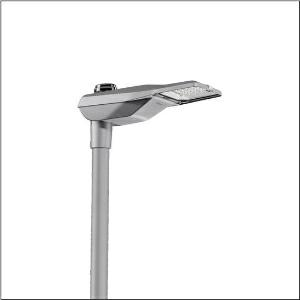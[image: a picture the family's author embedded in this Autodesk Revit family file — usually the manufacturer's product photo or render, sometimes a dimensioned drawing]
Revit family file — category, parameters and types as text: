
# Revit family: streetlight_sl_21_micro___st1_0a_5xe5d37n08db_4323
name_source: partatom
category: Lighting Fixtures
units: mm (PartAtom-declared; Revit-internal decimal feet)

## family parameters
Cut with Voids When Loaded = No
Host = Face
Light Source = No
Part Type = Normal
Room Calculation Point = No
Round Connector Dimension = Use Diameter
Shared = No

## types (1)
- --- (1 x LED, 5110 lm, 39.1 W, 3000K)
    Apparent Load = 39 VA
    CIE Flux Codes = 37 72 97 100 100
    Color Rendering = 70
    Color Temperature = 3000K
    Default Elevation = 1800 mm
    Description = Streetlight SL 21 micro, mast luminaire, primary light control with lens, of PMMA, primary optical cover: cover, of toughened safety glass, transparent, light distribution: ST1.0a, light emission: direct distribution, primary light characteristic: asymmetric, installation type: post-top, LED, 3G 1.5mm², High Power LED, rated luminous flux: 5.110lm, luminous efficacy: 131lm/W, light colour: 730, colour temperature: 3000K, control: overheat protection, presetting dimming linear, constant luminous flux control, time-dependent luminous flux control, flexible luminous flux parameterisation, mains connection: 230..240V, AC, 50/60Hz, connection cable pre-assembled, cable length: 6,5m, wiring characteristics: H07RN-F, start of lifetime: 39W, end of service life: 41W, reduction: 18W, luminaire housing, of diecast aluminium (EN AC-44300), powder-coated, Siteco® metallic grey (DB 702S), corrosivity category C5 mid according to DIN EN ISO 12944, multi-level sealing system, sealing non-destructively replaceable, inclination adjustable: 0°, 5°, 10°, 15°, length: 528mm, width: 235mm, height: 110mm, spigot size: 76/60mm (post-top), protection rating (complete): IP66, insulation class (complete): insulation class I (protective earthing), certification: CE, ENEC, ENEC+, VDE, impact resistance: IK09, permissible operating ambient temperature for outdoor applications: -40..+50°C, standard-compliant lighting for roads and squares, packaging unit: 1 piece

Light Distribution: ST1.0a
    Height = 110 mm
    Lamp = 1 x LED
    Lamp Light Flux = 5110 lm
    Lamp Power = 39.1 W
    Lamp count = 1
    Length = 528 mm
    Luminous efficacy = 131 lm/W
    Manufacturer = Siteco
    ModVariant = No
    Model = 5XE5D37N08DB
    Number of Poles = 1
    OnlyDefault = Yes
    Power Factor = 1
    Product Name = Streetlight SL 21 micro | ST1.0a
    Product group = mast luminaire | pylon top
    ProductGroupID = 6100
    Protection Class = Protection class I
    Protection Degree = IP 66
    RLX_Detail_Level = 1
    RLX_Emergency_Light_Flux = 0 lm
    RLX_Emergency_Type = 0
    RLX_Emergency_Type_DB = No
    RlxData = <blob elided: 99197 chars, md5=05ac353c>
    Socket = socket
    Standby Power = 0 W
    System Light Flux = 5110 lm
    System Power = 39 W
    Type Comments = factory setting: luminous flux: 100 % | dim-lin: 254 | 765 mA
    Type Image = l_1294375.jpg
    URL = http://relux.com
    VarID = @adj_085923
    Voltage = 0 V
    Weight = 0.00 kg
    Width = 235 mm

## geometry (parser evidence)
native form markers: Blend x4, Sweep x11
no freeform markers — native parametric forms only
